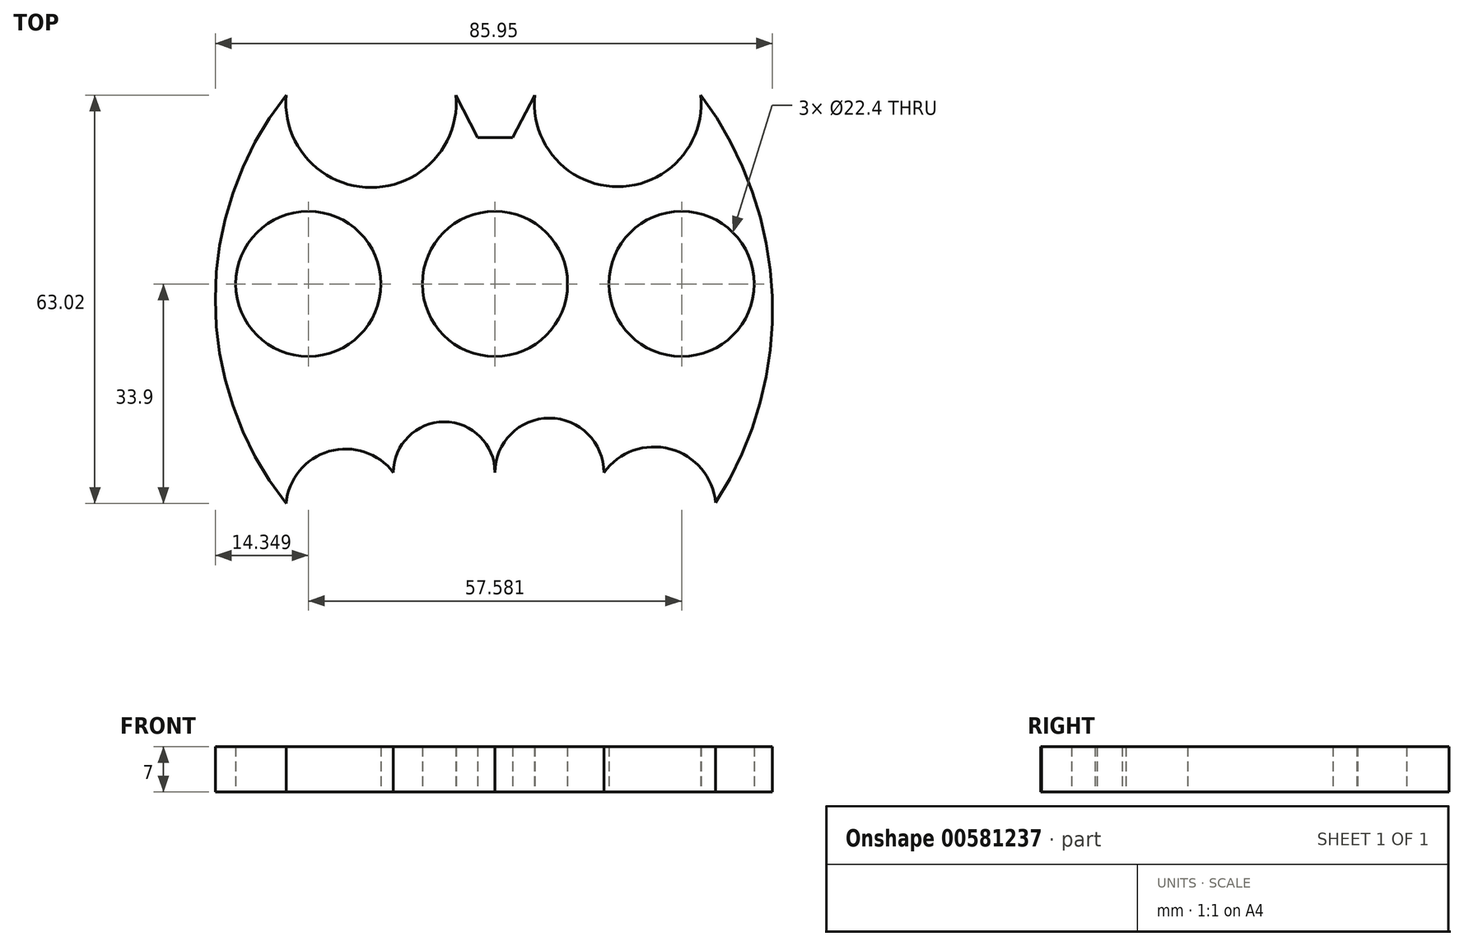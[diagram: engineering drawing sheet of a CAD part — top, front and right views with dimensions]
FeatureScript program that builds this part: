
annotation { "Feature Type Name" : "Feature", "Feature Type Description" : "" }
export const myFeature = defineFeature(function(context is Context, id is Id, definition is map)
    precondition{}
    {
        {
            var Q0;
            Q0=qCreatedBy(makeId("Top.planeOp"),FACE);
            var sketch = newSketch(context, id + "F0", { "sketchPlane" : qUnion([Q0])});
            skCircle(sketch, "E0", {"center": v(0, 0) * mm, "radius": 11.2 * mm});
            skArc(sketch, "E1", {"start": v(-32.22, 29.12) * mm, "mid": v(-19.11, 14.87) * mm, "end": v(-6, 29.12) * mm});
            skArc(sketch, "E2", {"start": v(-32.22, 29.12) * mm, "mid": v(-43.14, -2.39) * mm, "end": v(-32.22, -33.9) * mm});
            skLineSegment(sketch, "E3", {"start": v(6.13, 29.12) * mm, "end": v(2.73, 22.56) * mm});
            skLineSegment(sketch, "E4", {"start": v(-2.65, 22.56) * mm, "end": v(-6, 29.12) * mm});
            skLineSegment(sketch, "E5", {"start": v(-2.65, 22.56) * mm, "end": v(2.73, 22.56) * mm});
            skCircle(sketch, "E6", {"center": v(-28.8, 0) * mm, "radius": 11.2 * mm});
            skCircle(sketch, "E7.2.0", {"center": v(28.8, 0) * mm, "radius": 11.2 * mm});
            skLineSegment(sketch, "E7.anchor1", {"start": v(0, 0) * mm, "end": v(-28.8, 0) * mm, "construction": true});
            skLineSegment(sketch, "E7.anchor2", {"start": v(0, 0) * mm, "end": v(28.8, 0) * mm, "construction": true});
            skLineSegment(sketch, "E8.1.0", {"start": v(0, -11.2) * mm, "end": v(0, -29.12) * mm});
            skLineSegment(sketch, "E8.anchor1", {"start": v(0, 0) * mm, "end": v(0, 11.2) * mm, "construction": true});
            skLineSegment(sketch, "E8.anchor2", {"start": v(0, 0) * mm, "end": v(0, -11.2) * mm, "construction": true});
            skArc(sketch, "E9", {"start": v(-15.66, -29.12) * mm, "mid": v(-25.58, -25.84) * mm, "end": v(-32.22, -33.9) * mm});
            skArc(sketch, "E10", {"start": v(16.81, -29.12) * mm, "mid": v(8.4, -20.72) * mm, "end": v(0, -29.12) * mm});
            skArc(sketch, "E11", {"start": v(0, -29.12) * mm, "mid": v(-7.83, -21.3) * mm, "end": v(-15.66, -29.12) * mm});
            skArc(sketch, "E12", {"start": v(6.13, 29.12) * mm, "mid": v(18.94, 15) * mm, "end": v(31.76, 29.12) * mm});
            skArc(sketch, "E13", {"start": v(34.06, -33.77) * mm, "mid": v(42.78, -1.96) * mm, "end": v(31.76, 29.12) * mm});
            skArc(sketch, "E14", {"start": v(34.06, -33.77) * mm, "mid": v(27.04, -25.48) * mm, "end": v(16.81, -29.12) * mm});
            skSolve(sketch);
        }
        {
            var Q0;
            {var subQ0=sQuery(id+"F0.wireOp",EDGE,"E1");var subQ1=sQuery(id+"F0.wireOp",EDGE,"wIcN4tQ4-OL0U-KsKI-jLEZ-Zv3lfoWd9Mhj");var subQ2=makeQuery(id+"F0.imprint","INTERSECT",VERTEX,{"disambiguationData":[OD(0.0)],"derivedFrom":[subQ1,subQ0]});Q0=makeQuery(id+"F0.imprint","IMPRINT",FACE,{"disambiguationData":[TD([[makeQuery(id+"F0.imprint","IMPRINT",EDGE,{"disambiguationData":[TD([[subQ2,-1.0]])],"derivedFrom":subQ1}),1.0]])]});}
            var Q1;
            {var subQ0=sQuery(id+"F0.wireOp",EDGE,"5JRACpp4-PRD0-rouX-UC56-cgVRFbCboe1I");var subQ1=sQuery(id+"F0.wireOp",EDGE,"uIxHRKaC-fXGP-C11L-FGjw-L1SI6bDexqCe");var subQ2=makeQuery(id+"F0.imprint","INTERSECT",VERTEX,{"disambiguationData":[OD(0.0)],"derivedFrom":[subQ1,subQ0]});Q1=makeQuery(id+"F0.imprint","IMPRINT",FACE,{"disambiguationData":[TD([[makeQuery(id+"F0.imprint","IMPRINT",EDGE,{"disambiguationData":[TD([[subQ2,1.0]])],"derivedFrom":subQ1}),1.0]])]});}
            var Q2;
            Q2=makeQuery(id+"F0.imprint","IMPRINT",FACE,{"disambiguationData":[TD([[makeQuery(id+"F0.imprint","IMPRINT",EDGE,{"derivedFrom":sQuery(id+"F0.wireOp",EDGE,"E0")}),-1.0]])]});
            extrude(context, id + "F1", {"entities" : qUnion([Q0, Q1, Q2]), "depth" : 7 * mm, "offsetDistance" : 25 * mm});
        }
        {
            var Q0;
            Q0 = qSketchRegion(id + "F0", true);
            extrude(context, id + "F2", {"entities" : qUnion([Q0]), "operationType" : NewBodyOperationType.ADD, "depth" : 7 * mm, "offsetDistance" : 25 * mm});
        }
    });
